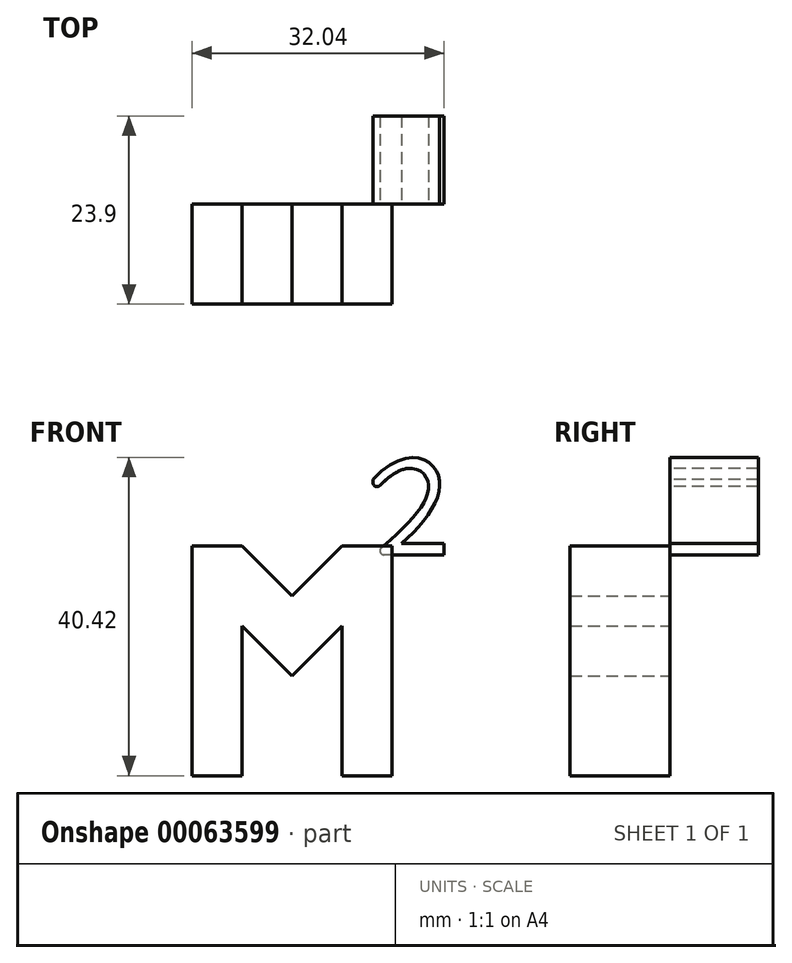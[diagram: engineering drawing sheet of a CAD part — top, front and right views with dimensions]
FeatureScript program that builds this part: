
annotation { "Feature Type Name" : "Feature", "Feature Type Description" : "" }
export const myFeature = defineFeature(function(context is Context, id is Id, definition is map)
    precondition{}
    {
        {
            var Q0;
            Q0=qCreatedBy(makeId("Front.planeOp"),FACE);
            var sketch = newSketch(context, id + "F0", { "sketchPlane" : qUnion([Q0])});
            skLineSegment(sketch, "E0", {"start": v(-25.4, 0) * mm, "end": v(-25.4, 29.21) * mm});
            skLineSegment(sketch, "E1", {"start": v(-25.4, 29.2) * mm, "end": v(-19.05, 29.2) * mm});
            skLineSegment(sketch, "E2", {"start": v(-19.05, 29.21) * mm, "end": v(-12.7, 22.86) * mm});
            skLineSegment(sketch, "E3", {"start": v(-25.4, 0) * mm, "end": v(-19.05, 0) * mm});
            skLineSegment(sketch, "E4", {"start": v(-19.05, 0) * mm, "end": v(-19.05, 19.05) * mm});
            skLineSegment(sketch, "E5", {"start": v(-19.05, 19.05) * mm, "end": v(-12.7, 12.7) * mm});
            skLineSegment(sketch, "E6", {"start": v(-12.7, 12.7) * mm, "end": v(-12.7, 22.86) * mm, "construction": true});
            skLineSegment(sketch, "E7.MirrorCS", {"start": v(-6.35, 29.21) * mm, "end": v(-12.7, 22.86) * mm});
            skLineSegment(sketch, "E8.MirrorCS", {"start": v(0, 29.21) * mm, "end": v(-6.35, 29.21) * mm});
            skLineSegment(sketch, "E9.MirrorCS", {"start": v(0, 0) * mm, "end": v(0, 29.21) * mm});
            skLineSegment(sketch, "E10.MirrorCS", {"start": v(0, 0) * mm, "end": v(-6.35, 0) * mm});
            skLineSegment(sketch, "E11.MirrorCS", {"start": v(-6.35, 0) * mm, "end": v(-6.35, 19.05) * mm});
            skLineSegment(sketch, "E12.MirrorCS", {"start": v(-6.35, 19.05) * mm, "end": v(-12.7, 12.7) * mm});
            skSolve(sketch);
        }
        {
            var Q0;
            Q0 = qSketchRegion(id + "F0", true);
            extrude(context, id + "F1", {"entities" : qUnion([Q0]), "depth" : 12.7 * mm});
        }
        {
            var Q0;
            Q0=qCreatedBy(makeId("Front.planeOp"),FACE);
            var sketch = newSketch(context, id + "F2", { "sketchPlane" : qUnion([Q0])});
            skLineSegment(sketch, "E13", {"start": v(6.64, 28.06) * mm, "end": v(-2.4, 28.06) * mm});
            skFitSpline(sketch, "E14", {"points": [v(-2.4, 28.06) * mm, v(4.6, 37.28) * mm, v(-2.4, 35.88) * mm], "startDerivative": vector(24.25, 20.28) * mm, "endDerivative": vector(-26.39, -32.15) * mm});
            skLineSegment(sketch, "E15", {"start": v(6.64, 29.48) * mm, "end": v(1.24, 29.48) * mm});
            skFitSpline(sketch, "E16", {"points": [v(1.24, 29.48) * mm, v(5.91, 38.1) * mm, v(-2.4, 37.6) * mm], "startDerivative": vector(18.04, 15.65) * mm, "endDerivative": vector(-25.89, -27.99) * mm});
            skLineSegment(sketch, "E17", {"start": v(-2.4, 37.6) * mm, "end": v(-2.4, 35.88) * mm});
            skLineSegment(sketch, "E18", {"start": v(6.64, 29.48) * mm, "end": v(6.64, 28.06) * mm});
            skSolve(sketch);
        }
        {
            var Q0;
            Q0 = qSketchRegion(id + "F2", true);
            extrude(context, id + "F3", {"entities" : qUnion([Q0]), "operationType" : NewBodyOperationType.ADD, "oppositeDirection" : true, "depth" : 11.2 * mm});
        }
        {
            var Q0;
            Q0=makeQuery(id+"F3.opExtrude","SWEPT_EDGE",EDGE,{"disambiguationData":[OSD([sQuery(id+"F2.wireOp",EDGE,"E13"),sQuery(id+"F2.wireOp",EDGE,"E14")])]});
            var Q1;
            Q1=makeQuery(id+"F3.opExtrude","SWEPT_EDGE",EDGE,{"disambiguationData":[OSD([sQuery(id+"F2.wireOp",EDGE,"E14"),sQuery(id+"F2.wireOp",EDGE,"E17")])]});
            fillet(context, id + "F4", {"entities" : qUnion([Q0, Q1]), "radius" : 0.5 * mm, "tangentPropagation" : true, "allowEdgeOverflow" : false});
        }
    });
